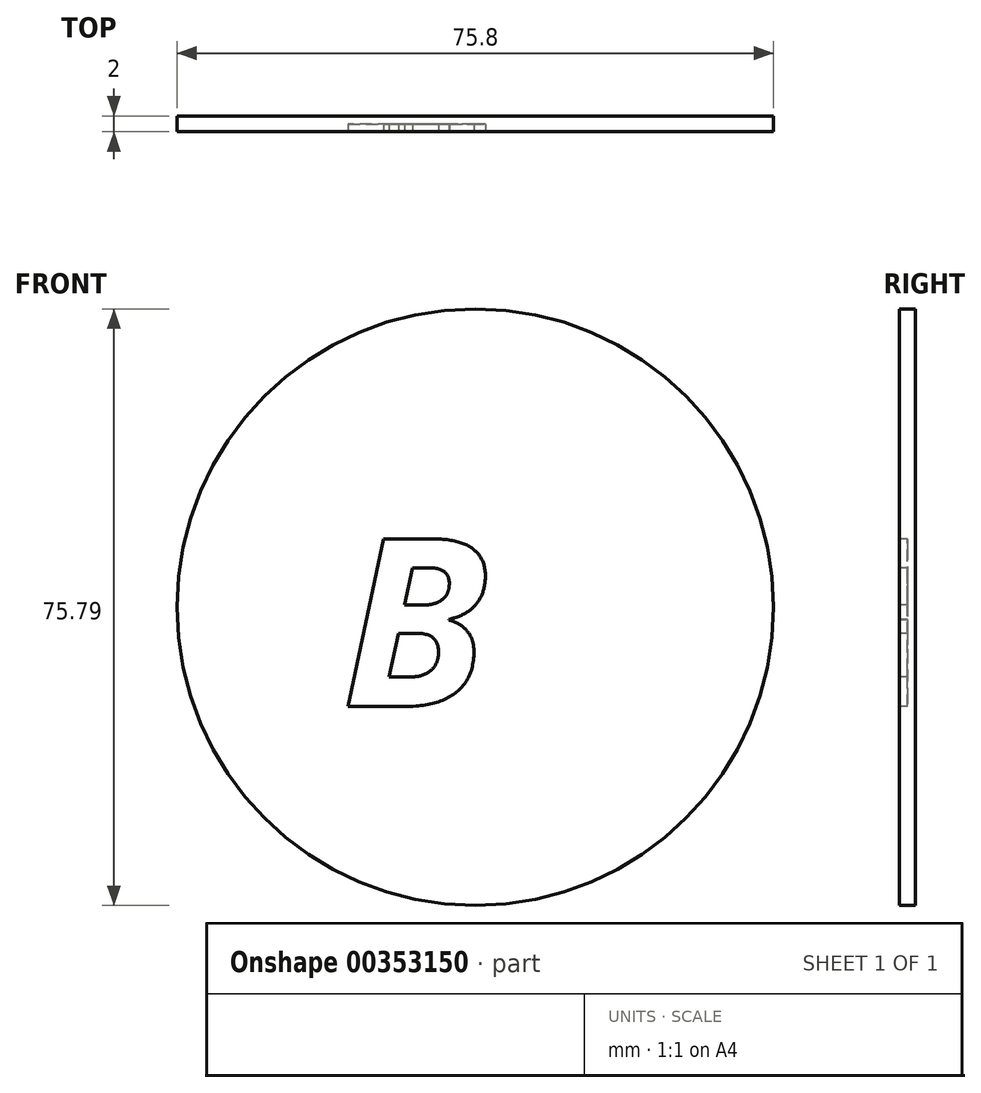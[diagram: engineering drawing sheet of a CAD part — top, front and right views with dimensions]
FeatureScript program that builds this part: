
annotation { "Feature Type Name" : "Feature", "Feature Type Description" : "" }
export const myFeature = defineFeature(function(context is Context, id is Id, definition is map)
    precondition{}
    {
        {
            var Q0;
            Q0=qCreatedBy(makeId("Front.planeOp"),FACE);
            var sketch = newSketch(context, id + "F0", { "sketchPlane" : qUnion([Q0])});
            skCircle(sketch, "E0", {"center": v(-39.48, 36.9) * mm, "radius": 37.9 * mm});
            skSolve(sketch);
        }
        {
            var Q0;
            Q0 = qSketchRegion(id + "F0", true);
            var Q1;
            Q1=sQuery(id+"F0.wireOp",EDGE,"E0");
            extrude(context, id + "F1", {"entities" : qUnion([Q0]), "surfaceEntities" : qUnion([Q1]), "depth" : 2 * mm});
        }
        {
            var Q0;
            Q0=makeQuery(id+"F1.opExtrude","CAP_FACE",FACE,{"disambiguationData":[OSD([sQuery(id+"F0.wireOp",EDGE,"E0")])],"isStart":false});
            var sketch = newSketch(context, id + "F2", { "sketchPlane" : qUnion([Q0])});
            skText(sketch, "E1", { "text": "B", "fontName": "OpenSans-BoldItalic.ttf"});
            const initialGuessF2  = {"E1": [-0.0564, 0.0243, 1, 0, 0.02146]};
            skSetInitialGuess(sketch, initialGuessF2);
            skSolve(sketch);
        }
        {
            var Q0;
            Q0 = qSketchRegion(id + "F2", true);
            extrude(context, id + "F3", {"entities" : qUnion([Q0]), "operationType" : NewBodyOperationType.REMOVE, "oppositeDirection" : true, "depth" : 1 * mm});
        }
    });
